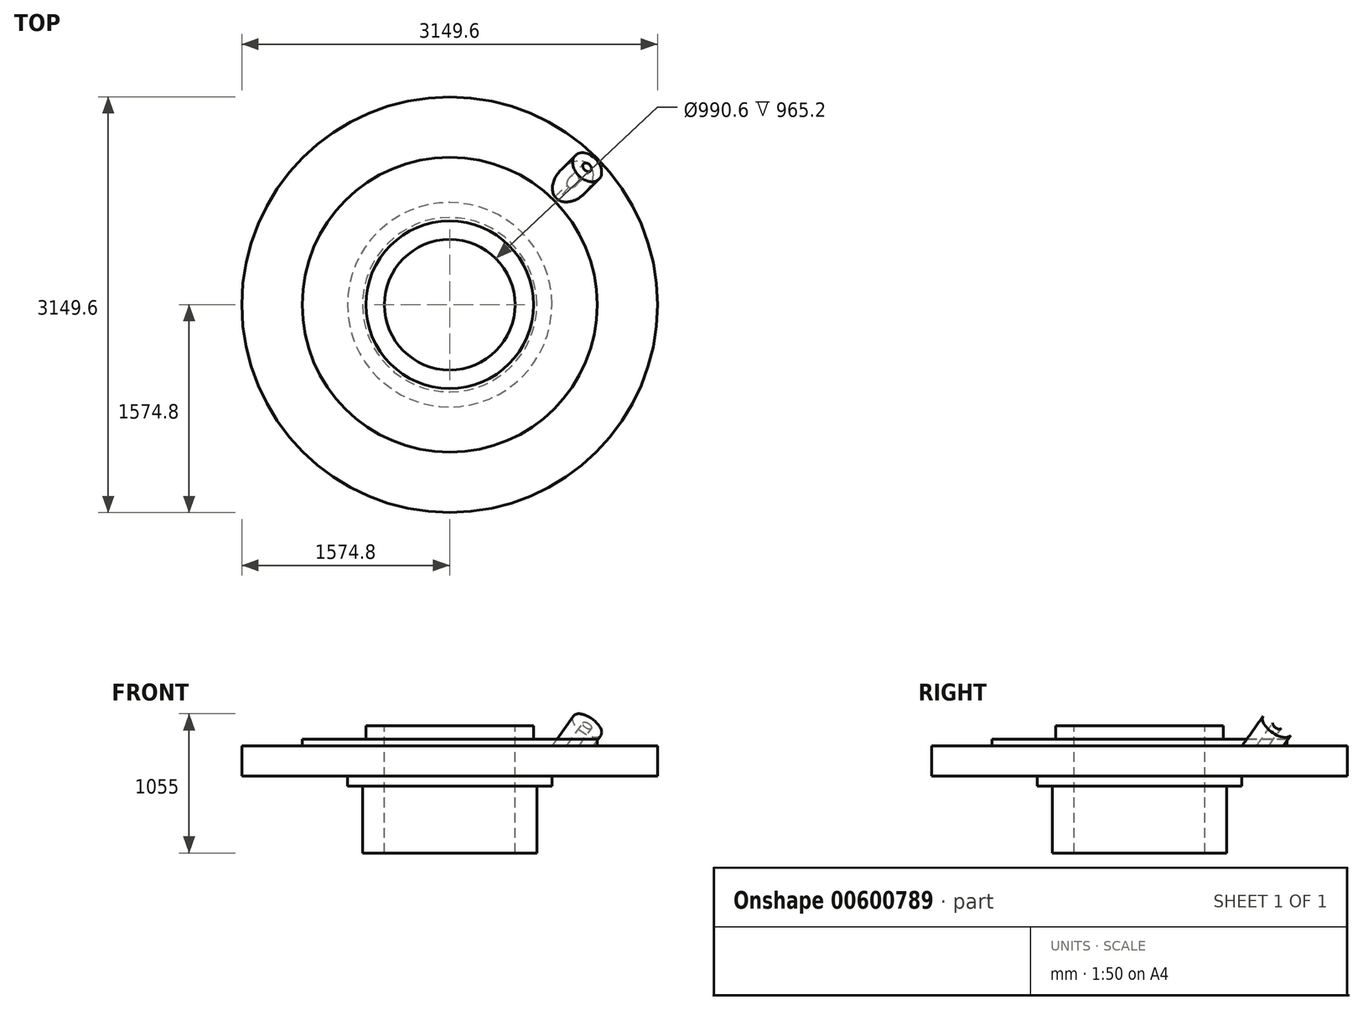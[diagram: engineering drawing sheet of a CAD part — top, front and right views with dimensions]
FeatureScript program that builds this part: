
annotation { "Feature Type Name" : "Feature", "Feature Type Description" : "" }
export const myFeature = defineFeature(function(context is Context, id is Id, definition is map)
    precondition{}
    {
        {
            var Q0;
            Q0=qCreatedBy(makeId("Front.planeOp"),FACE);
            var sketch = newSketch(context, id + "F0", { "sketchPlane" : qUnion([Q0])});
            skLineSegment(sketch, "E0.bottom", {"start": v(0, 0) * mm, "end": v(635, 0) * mm});
            skLineSegment(sketch, "E0.top", {"start": v(0, 101.6) * mm, "end": v(635, 101.6) * mm});
            skLineSegment(sketch, "E0.left", {"start": v(0, 0) * mm, "end": v(0, 101.6) * mm});
            skLineSegment(sketch, "E0.right", {"start": v(635, 0) * mm, "end": v(635, 101.6) * mm});
            skLineSegment(sketch, "E1.bottom", {"start": v(0, 0) * mm, "end": v(1117.6, 0) * mm});
            skLineSegment(sketch, "E1.top", {"start": v(0, -50.8) * mm, "end": v(1117.6, -50.8) * mm});
            skLineSegment(sketch, "E1.left", {"start": v(0, 0) * mm, "end": v(0, -50.8) * mm});
            skLineSegment(sketch, "E1.right", {"start": v(1117.6, 0) * mm, "end": v(1117.6, -50.8) * mm});
            skLineSegment(sketch, "E2.bottom", {"start": v(0, -50.8) * mm, "end": v(1574.8, -50.8) * mm});
            skLineSegment(sketch, "E2.top", {"start": v(0, -279.4) * mm, "end": v(1574.8, -279.4) * mm});
            skLineSegment(sketch, "E2.right", {"start": v(1574.8, -50.8) * mm, "end": v(1574.8, -279.4) * mm});
            skLineSegment(sketch, "E3", {"start": v(0, 0) * mm, "end": v(0, -279.4) * mm});
            skLineSegment(sketch, "E4.bottom", {"start": v(0, -279.4) * mm, "end": v(774.7, -279.4) * mm});
            skLineSegment(sketch, "E4.top", {"start": v(0, -355.6) * mm, "end": v(774.7, -355.6) * mm});
            skLineSegment(sketch, "E4.left", {"start": v(0, -279.4) * mm, "end": v(0, -355.6) * mm});
            skLineSegment(sketch, "E4.right", {"start": v(774.7, -279.4) * mm, "end": v(774.7, -355.6) * mm});
            skLineSegment(sketch, "E5", {"start": v(0, 427.51) * mm, "end": v(0, -948.87) * mm});
            skLineSegment(sketch, "E6.bottom", {"start": v(0, -355.6) * mm, "end": v(660.4, -355.6) * mm});
            skLineSegment(sketch, "E6.top", {"start": v(0, -863.6) * mm, "end": v(660.4, -863.6) * mm});
            skLineSegment(sketch, "E6.left", {"start": v(0, -355.6) * mm, "end": v(0, -863.6) * mm});
            skLineSegment(sketch, "E6.right", {"start": v(660.4, -355.6) * mm, "end": v(660.4, -863.6) * mm});
            skSolve(sketch);
        }
        {
            var Q0;
            Q0 = qSketchRegion(id + "F0", true);
            var Q1;
            Q1=sQuery(id+"F0.wireOp",EDGE,"E5");
            revolve(context, id + "F1", {"entities" : qUnion([Q0]), "axis" : qUnion([Q1]), "revolveType" : RevolveType.FULL});
        }
        {
            var Q0;
            Q0=makeQuery(id+"F1.opRevolve","SWEPT_FACE",FACE,{"disambiguationData":[OSD([sQuery(id+"F0.wireOp",EDGE,"E0.top")])]});
            var sketch = newSketch(context, id + "F2", { "sketchPlane" : qUnion([Q0])});
            skPoint(sketch, "E7", {"position": v(0, 0) * mm});
            skSolve(sketch);
        }
        {
            var Q0;
            Q0=sQuery(id+"F2.wireOp",VERTEX,"E7");
            var Q1;
            Q1=makeQuery(id+"F1.opRevolve","SWEPT_BODY",BODY,{"disambiguationData":[OSD([sQuery(id+"F0.wireOp",EDGE,"E0.top"),sQuery(id+"F0.wireOp",EDGE,"E0.right"),sQuery(id+"F0.wireOp",EDGE,"E1.bottom"),sQuery(id+"F0.wireOp",EDGE,"E1.right"),sQuery(id+"F0.wireOp",EDGE,"E2.bottom"),sQuery(id+"F0.wireOp",EDGE,"E2.top"),sQuery(id+"F0.wireOp",EDGE,"E2.right"),sQuery(id+"F0.wireOp",EDGE,"E4.top"),sQuery(id+"F0.wireOp",EDGE,"E4.right"),sQuery(id+"F0.wireOp",EDGE,"E5"),sQuery(id+"F0.wireOp",EDGE,"E6.top"),sQuery(id+"F0.wireOp",EDGE,"E6.left"),sQuery(id+"F0.wireOp",EDGE,"E6.right")])]});
            hole(context, id + "F3", {"style" : HoleStyle.SIMPLE, "endStyle" : HoleEndStyle.THROUGH, "holeDiameter" : 990.6 * mm, "majorDiameter" : 6.35 * mm, "isTappedThrough" : true, "tappedDepth" : 12.7 * mm, "tapClearance" : 3, "locations" : qUnion([Q0]), "scope" : qUnion([Q1])});
        }
        {
            var Q0;
            Q0=makeQuery(id+"F1.opRevolve","SWEPT_FACE",FACE,{"disambiguationData":[OSD([sQuery(id+"F0.wireOp",EDGE,"E2.bottom")])]});
            var sketch = newSketch(context, id + "F4", { "sketchPlane" : qUnion([Q0])});
            skLineSegment(sketch, "E8", {"start": v(0, 0) * mm, "end": v(0, 1574.8) * mm});
            skLineSegment(sketch, "E9", {"start": v(0, 0) * mm, "end": v(1574.8, 0) * mm});
            skLineSegment(sketch, "E10", {"start": v(0, 0) * mm, "end": v(1113.55, 1113.55) * mm});
            skSolve(sketch);
        }
        {
            var Q0;
            Q0=sQuery(id+"F4.wireOp",EDGE,"E10");
            cPlane(context, id + "F5", {"entities" : qUnion([Q0]), "cplaneType" : CPlaneType.LINE_ANGLE, "offset" : 25.4 * mm, "angle" : 90 * degree, "width" : 152.4 * mm, "height" : 152.4 * mm});
        }
        {
            var Q0;
            Q0=qCreatedBy(id+"F5.planeOp",FACE);
            var sketch = newSketch(context, id + "F6", { "sketchPlane" : qUnion([Q0])});
            skLineSegment(sketch, "E11", {"start": v(1615.22, 243.62) * mm, "end": v(837.72, -533.88) * mm, "construction": true});
            skLineSegment(sketch, "E12", {"start": v(1473.2, 101.6) * mm, "end": v(1383.4, 191.4) * mm});
            skPoint(sketch, "E13.endSnap0", {"position": v(1226.47, -145.13) * mm});
            skLineSegment(sketch, "E14", {"start": v(1383.4, 191.4) * mm, "end": v(1141.9, -50.1) * mm});
            skPoint(sketch, "E15.orphan", {"position": v(1192, 0) * mm});
            skLineSegment(sketch, "E16", {"start": v(1141.9, -50.1) * mm, "end": v(1321.5, -50.1) * mm});
            skLineSegment(sketch, "E17", {"start": v(1473.2, 101.6) * mm, "end": v(1321.5, -50.1) * mm});
            skSolve(sketch);
        }
        {
            var Q0;
            Q0=makeQuery(id+"F6.imprint","IMPRINT",FACE,{"disambiguationData":[TD([[makeQuery(id+"F6.imprint","IMPRINT",EDGE,{"derivedFrom":sQuery(id+"F6.wireOp",EDGE,"E12")}),1.0]])]});
            var Q1;
            Q1 = qSketchRegion(id + "F8", true);
            var Q2;
            Q2=sQuery(id+"F6.wireOp",EDGE,"E11");
            revolve(context, id + "F7", {"operationType" : NewBodyOperationType.ADD, "entities" : qUnion([Q0, Q1]), "axis" : qUnion([Q2]), "revolveType" : RevolveType.FULL});
        }
        {
            var Q0;
            Q0=makeQuery(id+"F7.opRevolve","SWEPT_FACE",FACE,{"disambiguationData":[OSD([sQuery(id+"F6.wireOp",EDGE,"E12")])]});
            var sketch = newSketch(context, id + "F8", { "sketchPlane" : qUnion([Q0])});
            skPoint(sketch, "E18", {"position": v(559.95, 791.9) * mm});
            skSolve(sketch);
        }
        {
            var Q0;
            Q0=makeQuery(id+"F8.imprint","IMPRINT",FACE,{"disambiguationData":[TD([[makeQuery(id+"F8.imprint","IMPRINT",EDGE,{"derivedFrom":makeQuery(id+"F7.opRevolve","SWEPT_EDGE",EDGE,{"disambiguationData":[OSD([sQuery(id+"F6.wireOp",EDGE,"E12"),sQuery(id+"F6.wireOp",EDGE,"E14")])]})}),1.0]])]});
            var sketch = newSketch(context, id + "F9", { "sketchPlane" : qUnion([Q0])});
            skCircle(sketch, "E19", {"center": v(559.95, 791.9) * mm, "radius": 38.1 * mm});
            skSolve(sketch);
        }
        {
            var Q0;
            Q0=makeQuery(id+"F9.imprint","IMPRINT",FACE,{"disambiguationData":[TD([[makeQuery(id+"F9.imprint","IMPRINT",EDGE,{"derivedFrom":sQuery(id+"F9.wireOp",EDGE,"E19")}),1.0]])]});
            var Q1;
            Q1=makeQuery(id+"F1.opRevolve","SWEPT_FACE",FACE,{"disambiguationData":[OSD([sQuery(id+"F0.wireOp",EDGE,"E2.bottom")])]});
            extrude(context, id + "F10", {"entities" : qUnion([Q0]), "operationType" : NewBodyOperationType.REMOVE, "endBound" : BoundingType.UP_TO_SURFACE, "oppositeDirection" : true, "depth" : 25.4 * mm, "endBoundEntityFace" : qUnion([Q1]), "offsetDistance" : 25.4 * mm});
        }
    });
